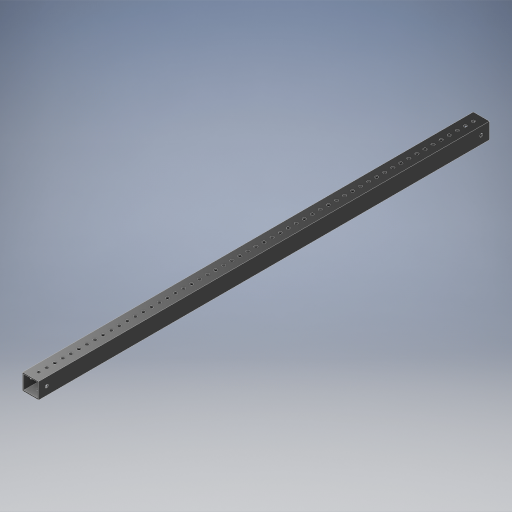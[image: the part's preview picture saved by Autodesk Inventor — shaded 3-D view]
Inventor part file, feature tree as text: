
AUTODESK INVENTOR PART (.ipt)
format: ipt  version: 2024.2 (Build 282272000, 272)  size: 862,208 bytes
history: native  units: in
note: dims shown in document units (in); Inventor stores cm internally (conversion verified against a paired STEP export)
features: other x13, extrude x9, hole x3, pattern_linear x3, mirror x3, sheet_metal_op x1, plane x1
ambient origin geometry x8: Origin, YZ Plane, XZ Plane, XY Plane, X Axis, Y Axis, Z Axis, Center Point
bodies: Solid1 (feature_tree)
feature tree (33):
  other  "Blocks"
  other  "Base Sketch"
  extrude  "Base"  Depth=1.0in
  extrude  "MAX Corner"  Depth=1.0in
  extrude  "MAX Corner Cut"  Depth=0.0625in
  extrude  "Scribe Lines"  Depth=0.0625in
  other  "Side Middle"
  other  "Top Middle"
  other  "Side Holes Sketch"
  hole  "Top Side Hole"  [1 undecoded]
  hole  "Mid Side Hole"  [1 undecoded]
  hole  "Btm Side Hole"  [1 undecoded]
  pattern_linear  "Side Holes"  Spacing1=0.04in  [1 undecoded]
  mirror  "Side Mirror"
  extrude  "MAXTube Hole"  Depth=0.04in
  extrude  "MAXTube Outside"  Depth=28.0in
  pattern_linear  "MAXTube Pattern"  Spacing1=0.0in  [1 undecoded]
  mirror  "MAXTube Mirror"
  extrude  "Left Top Hole"  Depth=28.0in
  extrude  "Mid Top Hole"  TaperAngle=0.0deg  [1 undecoded]
  extrude  "Right Top Hole"  TaperAngle=0.0deg  [1 undecoded]
  pattern_linear  "Top Holes"  Spacing1=0.005in  [1 undecoded]
  mirror  "Top Mirror"
  sheet_metal_op  "Corner"
  other  "MAXTube"
  plane  "Work Plane3"
  other  "Corner:5"
  other  "Corner:6"
  other  "Corner:7"
  other  "Corner:8"
  other  "MAXTube:1"
  other  "MAXTube:2"
  other  "MAXTube:3"
note: 8 required parameter values undecoded (feature->parameter linkage not recoverable at this tier; creation-order binding heuristic only, values carry confidence <= 0.55)
